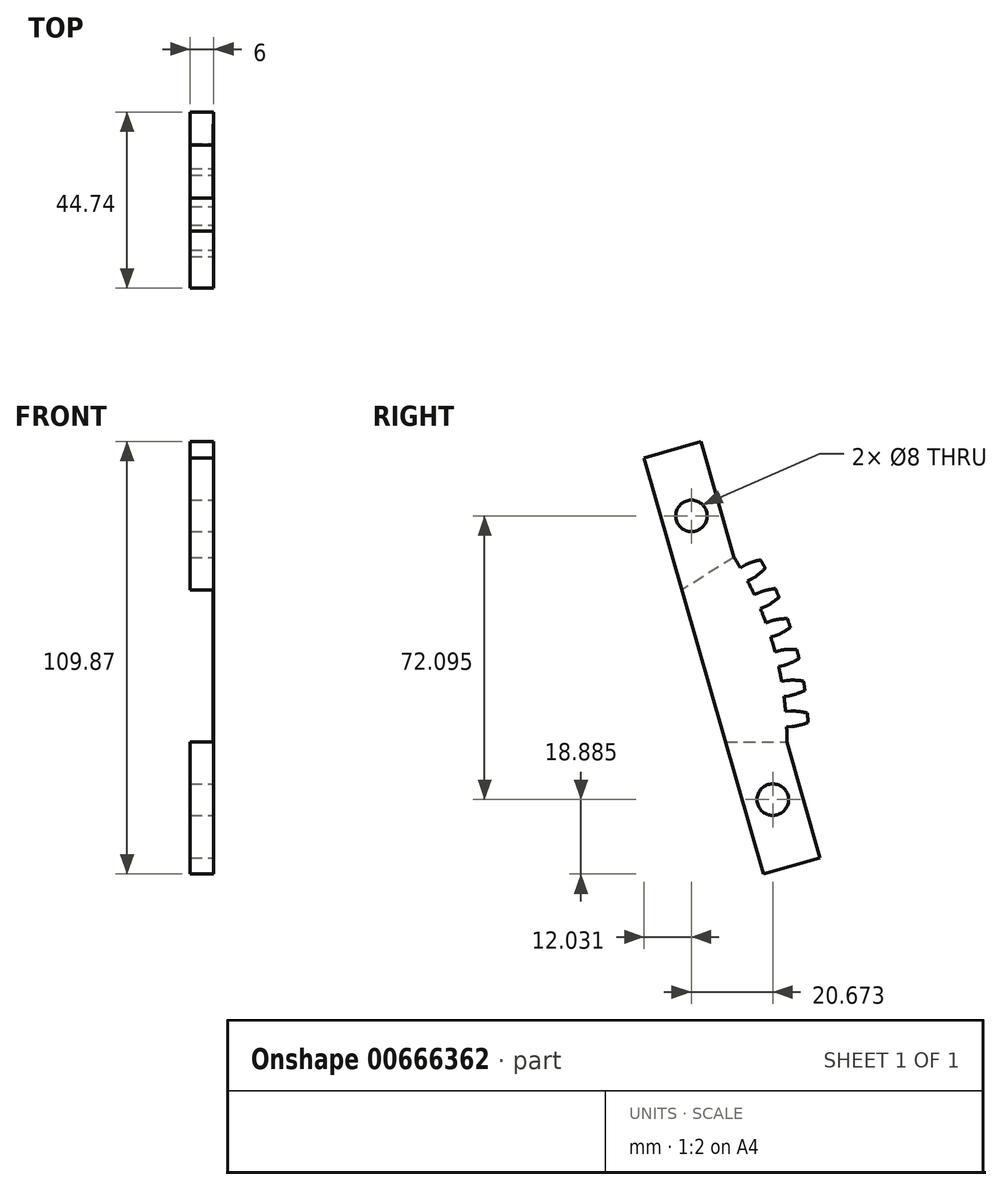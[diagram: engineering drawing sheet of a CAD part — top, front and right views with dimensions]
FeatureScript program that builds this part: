
annotation { "Feature Type Name" : "Feature", "Feature Type Description" : "" }
export const myFeature = defineFeature(function(context is Context, id is Id, definition is map)
    precondition{}
    {
        {
            assignVariable(context, id + "F0", {"name" : "NumberTeeth", "anyValue" : 72});
        }
        {
            assignVariable(context, id + "F1", {"name" : "GearThickness", "anyValue" : .236});
        }
        {
            var Q0;
            Q0=qCreatedBy(makeId("Right.planeOp"),FACE);
            var sketch = newSketch(context, id + "F2", { "sketchPlane" : qUnion([Q0])});
            skCircle(sketch, "E0", {"center": v(0, 0) * mm, "radius": 88.5 * mm});
            skCircle(sketch, "E1", {"center": v(0, 0) * mm, "radius": 89.9 * mm, "construction": true});
            skCircle(sketch, "E2", {"center": v(0, 0) * mm, "radius": 91.44 * mm, "construction": true});
            skCircle(sketch, "E3", {"center": v(0, 0) * mm, "radius": 93.98 * mm});
            skLineSegment(sketch, "E4", {"start": v(0, 0) * mm, "end": v(-89.9, 0) * mm, "construction": true});
            skLineSegment(sketch, "E5.1.0", {"start": v(0, 0) * mm, "end": v(-89.8, 4.5) * mm, "construction": true});
            skLineSegment(sketch, "E5.2.0", {"start": v(0, 0) * mm, "end": v(-89.46, 8.98) * mm, "construction": true});
            skLineSegment(sketch, "E5.3.0", {"start": v(0, 0) * mm, "end": v(-88.9, 13.44) * mm, "construction": true});
            skLineSegment(sketch, "E5.4.0", {"start": v(0, 0) * mm, "end": v(-88.12, 17.86) * mm, "construction": true});
            skLineSegment(sketch, "E5.5.0", {"start": v(0, 0) * mm, "end": v(-87.11, 22.24) * mm, "construction": true});
            skLineSegment(sketch, "E5.6.0", {"start": v(0, 0) * mm, "end": v(-85.9, 26.57) * mm, "construction": true});
            skLineSegment(sketch, "E5.7.0", {"start": v(0, 0) * mm, "end": v(-84.46, 30.83) * mm, "construction": true});
            skLineSegment(sketch, "E5.8.0", {"start": v(0, 0) * mm, "end": v(-82.81, 35.01) * mm, "construction": true});
            skLineSegment(sketch, "E5.9.0", {"start": v(0, 0) * mm, "end": v(-80.96, 39.1) * mm, "construction": true});
            skLineSegment(sketch, "E5.10.0", {"start": v(0, 0) * mm, "end": v(-78.9, 43.1) * mm, "construction": true});
            skLineSegment(sketch, "E5.11.0", {"start": v(0, 0) * mm, "end": v(-76.65, 47) * mm, "construction": true});
            skLineSegment(sketch, "E5.12.0", {"start": v(0, 0) * mm, "end": v(-74.2, 50.77) * mm, "construction": true});
            skLineSegment(sketch, "E5.13.0", {"start": v(0, 0) * mm, "end": v(-71.57, 54.41) * mm, "construction": true});
            skLineSegment(sketch, "E5.14.0", {"start": v(0, 0) * mm, "end": v(-68.77, 57.92) * mm, "construction": true});
            skLineSegment(sketch, "E5.anchor2", {"start": v(0, 0) * mm, "end": v(-68.77, 57.92) * mm, "construction": true});
            skLineSegment(sketch, "E6", {"start": v(-89.8, 4.5) * mm, "end": v(-90.02, 0) * mm, "construction": true});
            skLineSegment(sketch, "E7", {"start": v(-89.46, 8.98) * mm, "end": v(-90.36, 0.03) * mm, "construction": true});
            skLineSegment(sketch, "E8", {"start": v(-88.9, 13.44) * mm, "end": v(-90.91, 0.1) * mm, "construction": true});
            skLineSegment(sketch, "E9", {"start": v(-87.11, 22.24) * mm, "end": v(-92.67, 0.47) * mm, "construction": true});
            skLineSegment(sketch, "E10", {"start": v(-85.9, 26.57) * mm, "end": v(-93.86, 0.8) * mm, "construction": true});
            skLineSegment(sketch, "E11", {"start": v(-84.46, 30.83) * mm, "end": v(-95.25, 1.27) * mm, "construction": true});
            skLineSegment(sketch, "E12", {"start": v(-82.81, 35.01) * mm, "end": v(-96.82, 1.89) * mm, "construction": true});
            skLineSegment(sketch, "E13", {"start": v(-80.96, 39.1) * mm, "end": v(-98.56, 2.68) * mm, "construction": true});
            skLineSegment(sketch, "E14", {"start": v(-78.9, 43.1) * mm, "end": v(-100.45, 3.65) * mm, "construction": true});
            skLineSegment(sketch, "E15", {"start": v(-76.65, 47) * mm, "end": v(-102.5, 4.84) * mm, "construction": true});
            skLineSegment(sketch, "E16", {"start": v(-88.12, 17.86) * mm, "end": v(-91.69, 0.24) * mm, "construction": true});
            skLineSegment(sketch, "E17", {"start": v(-74.2, 50.77) * mm, "end": v(-104.66, 6.24) * mm, "construction": true});
            skLineSegment(sketch, "E18", {"start": v(-71.57, 54.41) * mm, "end": v(-106.94, 7.89) * mm, "construction": true});
            skLineSegment(sketch, "E19", {"start": v(-68.77, 57.92) * mm, "end": v(-109.31, 9.78) * mm, "construction": true});
            skLineSegment(sketch, "E20", {"start": v(0, 0) * mm, "end": v(-89.89, 1.96) * mm, "construction": true});
            skLineSegment(sketch, "E21", {"start": v(-88.5, 0) * mm, "end": v(-89.9, 0) * mm});
            skLineSegment(sketch, "E22.MirrorCS", {"start": v(-88.42, 3.86) * mm, "end": v(-89.82, 3.92) * mm});
            skFitSpline(sketch, "E23", {"points": [v(-89.9, 0) * mm, v(-90.02, 0) * mm, v(-90.36, 0.03) * mm, v(-90.91, 0.1) * mm, v(-91.69, 0.24) * mm, v(-92.67, 0.47) * mm, v(-93.86, 0.8) * mm, v(-95.25, 1.27) * mm, v(-96.82, 1.89) * mm, v(-98.56, 2.68) * mm, v(-100.45, 3.65) * mm, v(-102.5, 4.84) * mm, v(-104.66, 6.24) * mm, v(-106.94, 7.89) * mm, v(-109.31, 9.78) * mm], "startDerivative": vector(-0.31, 0) * mm, "endDerivative": vector(-3.2, 2.69) * mm});
            skLineSegment(sketch, "E24", {"start": v(-52.65, -37.94) * mm, "end": v(-109.31, 9.78) * mm, "construction": true});
            skFitSpline(sketch, "E25.MirrorCS", {"points": [v(-89.82, 3.92) * mm, v(-89.94, 3.92) * mm, v(-90.27, 3.91) * mm, v(-90.83, 3.86) * mm, v(-91.61, 3.76) * mm, v(-92.6, 3.58) * mm, v(-93.8, 3.3) * mm, v(-95.21, 2.89) * mm, v(-96.8, 2.34) * mm, v(-98.58, 1.63) * mm, v(-100.52, 0.73) * mm, v(-102.6, -0.36) * mm, v(-104.84, -1.67) * mm, v(-107.18, -3.22) * mm, v(-109.63, -5) * mm], "startDerivative": vector(-0.31, 0.01) * mm, "endDerivative": vector(-3.3, -2.55) * mm});
            skSolve(sketch);
        }
        {
            var Q0;
            {var subQ0=sQuery(id+"F2.wireOp",EDGE,"E0");var subQ27=makeQuery(id+"F2.imprint","INTERSECT",VERTEX,{"derivedFrom":[subQ0,sQuery(id+"F2.wireOp",EDGE,"10ea1024-8cf5-41f5-a75f-a634b86921f3.10.0")]});Q0=makeQuery(id+"F2.imprint","IMPRINT",FACE,{"disambiguationData":[TD([[makeQuery(id+"F2.imprint","IMPRINT",EDGE,{"disambiguationData":[TD([[subQ27,-1.0]])],"derivedFrom":subQ0}),1.0]])]});}
            var Q1;
            {var subQ0=sQuery(id+"F2.wireOp",EDGE,"10ea1024-8cf5-41f5-a75f-a634b86921f3.1.0");Q1=makeQuery(id+"F2.imprint","IMPRINT",FACE,{"disambiguationData":[TD([[makeQuery(id+"F2.imprint","IMPRINT",EDGE,{"derivedFrom":subQ0}),-1.0]])]});}
            var Q2;
            {var subQ7=sQuery(id+"F2.wireOp",EDGE,"10ea1024-8cf5-41f5-a75f-a634b86921f3.2.0");Q2=makeQuery(id+"F2.imprint","IMPRINT",FACE,{"disambiguationData":[TD([[makeQuery(id+"F2.imprint","IMPRINT",EDGE,{"derivedFrom":subQ7}),-1.0]])]});}
            var Q3;
            {var subQ8=sQuery(id+"F2.wireOp",EDGE,"10ea1024-8cf5-41f5-a75f-a634b86921f3.3.0");Q3=makeQuery(id+"F2.imprint","IMPRINT",FACE,{"disambiguationData":[TD([[makeQuery(id+"F2.imprint","IMPRINT",EDGE,{"derivedFrom":subQ8}),-1.0]])]});}
            var Q4;
            {var subQ2=sQuery(id+"F2.wireOp",EDGE,"10ea1024-8cf5-41f5-a75f-a634b86921f3.4.0");Q4=makeQuery(id+"F2.imprint","IMPRINT",FACE,{"disambiguationData":[TD([[makeQuery(id+"F2.imprint","IMPRINT",EDGE,{"derivedFrom":subQ2}),-1.0]])]});}
            var Q5;
            {var subQ8=sQuery(id+"F2.wireOp",EDGE,"10ea1024-8cf5-41f5-a75f-a634b86921f3.5.0");Q5=makeQuery(id+"F2.imprint","IMPRINT",FACE,{"disambiguationData":[TD([[makeQuery(id+"F2.imprint","IMPRINT",EDGE,{"derivedFrom":subQ8}),-1.0]])]});}
            var Q6;
            {var subQ3=sQuery(id+"F2.wireOp",EDGE,"10ea1024-8cf5-41f5-a75f-a634b86921f3.6.0");Q6=makeQuery(id+"F2.imprint","IMPRINT",FACE,{"disambiguationData":[TD([[makeQuery(id+"F2.imprint","IMPRINT",EDGE,{"derivedFrom":subQ3}),-1.0]])]});}
            var Q7;
            {var subQ0=sQuery(id+"F2.wireOp",EDGE,"10ea1024-8cf5-41f5-a75f-a634b86921f3.7.0");Q7=makeQuery(id+"F2.imprint","IMPRINT",FACE,{"disambiguationData":[TD([[makeQuery(id+"F2.imprint","IMPRINT",EDGE,{"derivedFrom":subQ0}),-1.0]])]});}
            var Q8;
            {var subQ5=sQuery(id+"F2.wireOp",EDGE,"10ea1024-8cf5-41f5-a75f-a634b86921f3.8.0");Q8=makeQuery(id+"F2.imprint","IMPRINT",FACE,{"disambiguationData":[TD([[makeQuery(id+"F2.imprint","IMPRINT",EDGE,{"derivedFrom":subQ5}),-1.0]])]});}
            var Q9;
            {var subQ1=sQuery(id+"F2.wireOp",EDGE,"10ea1024-8cf5-41f5-a75f-a634b86921f3.9.0");Q9=makeQuery(id+"F2.imprint","IMPRINT",FACE,{"disambiguationData":[TD([[makeQuery(id+"F2.imprint","IMPRINT",EDGE,{"derivedFrom":subQ1}),-1.0]])]});}
            var Q10;
            {var subQ5=sQuery(id+"F2.wireOp",EDGE,"10ea1024-8cf5-41f5-a75f-a634b86921f3.10.0");Q10=makeQuery(id+"F2.imprint","IMPRINT",FACE,{"disambiguationData":[TD([[makeQuery(id+"F2.imprint","IMPRINT",EDGE,{"derivedFrom":subQ5}),-1.0]])]});}
            var Q11;
            {var subQ8=sQuery(id+"F2.wireOp",EDGE,"10ea1024-8cf5-41f5-a75f-a634b86921f3.11.0");Q11=makeQuery(id+"F2.imprint","IMPRINT",FACE,{"disambiguationData":[TD([[makeQuery(id+"F2.imprint","IMPRINT",EDGE,{"derivedFrom":subQ8}),-1.0]])]});}
            var Q12;
            {var subQ2=sQuery(id+"F2.wireOp",EDGE,"10ea1024-8cf5-41f5-a75f-a634b86921f3.12.0");Q12=makeQuery(id+"F2.imprint","IMPRINT",FACE,{"disambiguationData":[TD([[makeQuery(id+"F2.imprint","IMPRINT",EDGE,{"derivedFrom":subQ2}),-1.0]])]});}
            var Q13;
            {var subQ3=sQuery(id+"F2.wireOp",EDGE,"10ea1024-8cf5-41f5-a75f-a634b86921f3.13.0");Q13=makeQuery(id+"F2.imprint","IMPRINT",FACE,{"disambiguationData":[TD([[makeQuery(id+"F2.imprint","IMPRINT",EDGE,{"derivedFrom":subQ3}),-1.0]])]});}
            var Q14;
            {var subQ0=sQuery(id+"F2.wireOp",EDGE,"10ea1024-8cf5-41f5-a75f-a634b86921f3.14.0");Q14=makeQuery(id+"F2.imprint","IMPRINT",FACE,{"disambiguationData":[TD([[makeQuery(id+"F2.imprint","IMPRINT",EDGE,{"derivedFrom":subQ0}),-1.0]])]});}
            var Q15;
            {var subQ6=sQuery(id+"F2.wireOp",EDGE,"10ea1024-8cf5-41f5-a75f-a634b86921f3.15.0");Q15=makeQuery(id+"F2.imprint","IMPRINT",FACE,{"disambiguationData":[TD([[makeQuery(id+"F2.imprint","IMPRINT",EDGE,{"derivedFrom":subQ6}),-1.0]])]});}
            var Q16;
            {var subQ5=sQuery(id+"F2.wireOp",EDGE,"10ea1024-8cf5-41f5-a75f-a634b86921f3.16.0");Q16=makeQuery(id+"F2.imprint","IMPRINT",FACE,{"disambiguationData":[TD([[makeQuery(id+"F2.imprint","IMPRINT",EDGE,{"derivedFrom":subQ5}),-1.0]])]});}
            var Q17;
            {var subQ7=sQuery(id+"F2.wireOp",EDGE,"10ea1024-8cf5-41f5-a75f-a634b86921f3.17.0");Q17=makeQuery(id+"F2.imprint","IMPRINT",FACE,{"disambiguationData":[TD([[makeQuery(id+"F2.imprint","IMPRINT",EDGE,{"derivedFrom":subQ7}),-1.0]])]});}
            var Q18;
            {var subQ5=sQuery(id+"F2.wireOp",EDGE,"10ea1024-8cf5-41f5-a75f-a634b86921f3.18.0");Q18=makeQuery(id+"F2.imprint","IMPRINT",FACE,{"disambiguationData":[TD([[makeQuery(id+"F2.imprint","IMPRINT",EDGE,{"derivedFrom":subQ5}),-1.0]])]});}
            var Q19;
            {var subQ8=sQuery(id+"F2.wireOp",EDGE,"10ea1024-8cf5-41f5-a75f-a634b86921f3.19.0");Q19=makeQuery(id+"F2.imprint","IMPRINT",FACE,{"disambiguationData":[TD([[makeQuery(id+"F2.imprint","IMPRINT",EDGE,{"derivedFrom":subQ8}),-1.0]])]});}
            var Q20;
            {var subQ8=sQuery(id+"F2.wireOp",EDGE,"E21");Q20=makeQuery(id+"F2.imprint","IMPRINT",FACE,{"disambiguationData":[TD([[makeQuery(id+"F2.imprint","IMPRINT",EDGE,{"derivedFrom":subQ8}),-1.0]])]});}
            extrude(context, id + "F3", {"entities" : qUnion([Q0, Q1, Q2, Q3, Q4, Q5, Q6, Q7, Q8, Q9, Q10, Q11, Q12, Q13, Q14, Q15, Q16, Q17, Q18, Q19, Q20]), "depth" : (getVariable(context, 'GearThickness')) * mm});
        }
        {
            var Q0;
            Q0=makeQuery(id+"F3.opExtrude","SWEPT_FACE",FACE,{"disambiguationData":[OSD([sQuery(id+"F2.wireOp",EDGE,"E25.MirrorCS")])]});
            var Q1;
            Q1=makeQuery(id+"F3.opExtrude","SWEPT_FACE",FACE,{"disambiguationData":[OSD([sQuery(id+"F2.wireOp",EDGE,"E23")])]});
            var Q2;
            Q2=makeQuery(id+"F3.opExtrude","SWEPT_FACE",FACE,{"disambiguationData":[OSD([sQuery(id+"F2.wireOp",EDGE,"E3")])]});
            var Q3;
            Q3=makeQuery(id+"F3.opExtrude","SWEPT_FACE",FACE,{"disambiguationData":[OSD([sQuery(id+"F2.wireOp",EDGE,"E22.MirrorCS")])]});
            var Q4;
            Q4=makeQuery(id+"F3.opExtrude","SWEPT_FACE",FACE,{"disambiguationData":[OSD([sQuery(id+"F2.wireOp",EDGE,"E21")])]});
            var Q5;
            Q5=makeQuery(id+"F3.opExtrude","SWEPT_FACE",FACE,{"disambiguationData":[OSD([sQuery(id+"F2.wireOp",EDGE,"E0")])]});
            circularPattern(context, id + "F4", {"faces" : qUnion([Q0, Q1, Q2, Q3, Q4]), "axis" : qUnion([Q5]), "angle" : 360 * degree, "instanceCount" : getVariable(context, 'NumberTeeth'), "equalSpace" : true, "patternType" : PatternType.FACE});
        }
        {
            var Q0;
            Q0=makeQuery(id+"F3.opExtrude","CAP_FACE",FACE,{"disambiguationData":[OSD([sQuery(id+"F2.wireOp",EDGE,"E0"),sQuery(id+"F2.wireOp",EDGE,"E3"),sQuery(id+"F2.wireOp",EDGE,"E21"),sQuery(id+"F2.wireOp",EDGE,"E22.MirrorCS"),sQuery(id+"F2.wireOp",EDGE,"E23"),sQuery(id+"F2.wireOp",EDGE,"E25.MirrorCS")])],"isStart":false});
            var sketch = newSketch(context, id + "F5", { "sketchPlane" : qUnion([Q0])});
            skArc(sketch, "E26", {"start": v(102.47, 0) * mm, "mid": v(-98.5, -28.24) * mm, "end": v(86.9, 54.3) * mm});
            skLineSegment(sketch, "E27", {"start": v(0, 0) * mm, "end": v(127.7, 79.8) * mm, "construction": true});
            skLineSegment(sketch, "E28", {"start": v(86.9, 54.3) * mm, "end": v(0, 0) * mm});
            skLineSegment(sketch, "E29", {"start": v(0, 0) * mm, "end": v(102.47, 0) * mm});
            skSolve(sketch);
        }
        {
            var Q0;
            Q0 = qSketchRegion(id + "F5", true);
            extrude(context, id + "F6", {"entities" : qUnion([Q0]), "operationType" : NewBodyOperationType.REMOVE, "oppositeDirection" : true, "depth" : 25.4 * mm, "offsetDistance" : 25.4 * mm});
        }
        {
            var Q0;
            Q0=makeQuery(id+"F3.opExtrude","CAP_FACE",FACE,{"disambiguationData":[OSD([sQuery(id+"F2.wireOp",EDGE,"E0"),sQuery(id+"F2.wireOp",EDGE,"E3"),sQuery(id+"F2.wireOp",EDGE,"E21"),sQuery(id+"F2.wireOp",EDGE,"E22.MirrorCS"),sQuery(id+"F2.wireOp",EDGE,"E23"),sQuery(id+"F2.wireOp",EDGE,"E25.MirrorCS")])],"isStart":false});
            var sketch = newSketch(context, id + "F7", { "sketchPlane" : qUnion([Q0])});
            skLineSegment(sketch, "E30", {"start": v(88.5, 0) * mm, "end": v(75.05, 46.9) * mm, "construction": true});
            skLineSegment(sketch, "E31", {"start": v(0, 0) * mm, "end": v(81.78, 23.45) * mm, "construction": true});
            skLineSegment(sketch, "E32", {"start": v(81.78, 23.45) * mm, "end": v(66.62, 76.32) * mm});
            skLineSegment(sketch, "E33", {"start": v(66.62, 76.32) * mm, "end": v(52.2, 72.18) * mm});
            skLineSegment(sketch, "E34", {"start": v(52.2, 72.18) * mm, "end": v(67.36, 19.31) * mm});
            skLineSegment(sketch, "E35.MirrorCS", {"start": v(82.52, -33.55) * mm, "end": v(67.36, 19.31) * mm});
            skLineSegment(sketch, "E36.MirrorCS", {"start": v(96.94, -29.42) * mm, "end": v(82.52, -33.55) * mm});
            skLineSegment(sketch, "E37.MirrorCS", {"start": v(81.78, 23.45) * mm, "end": v(96.94, -29.42) * mm});
            skCircle(sketch, "E38", {"center": v(84.9, -14.67) * mm, "radius": 4 * mm});
            skLineSegment(sketch, "E39", {"start": v(89.73, -31.49) * mm, "end": v(77.55, 11) * mm, "construction": true});
            skCircle(sketch, "E40.MirrorC", {"center": v(64.23, 57.43) * mm, "radius": 4 * mm});
            skSolve(sketch);
        }
        {
            var Q0;
            {var subQ3=sQuery(id+"F7.wireOp",EDGE,"E33");Q0=makeQuery(id+"F7.imprint","IMPRINT",FACE,{"disambiguationData":[TD([[makeQuery(id+"F7.imprint","IMPRINT",EDGE,{"derivedFrom":subQ3}),1.0]])]});}
            var Q1;
            {var subQ0=sQuery(id+"F7.wireOp",EDGE,"E36.MirrorCS");Q1=makeQuery(id+"F7.imprint","IMPRINT",FACE,{"disambiguationData":[TD([[makeQuery(id+"F7.imprint","IMPRINT",EDGE,{"derivedFrom":subQ0}),-1.0]])]});}
            extrude(context, id + "F8", {"entities" : qUnion([Q0, Q1]), "operationType" : NewBodyOperationType.ADD, "oppositeDirection" : true, "depth" : 6 * mm, "offsetDistance" : 25.4 * mm});
        }
        {
            var Q0;
            {var subQ0=sQuery(id+"F7.wireOp",EDGE,"E35.MirrorCS");var subQ1=sQuery(id+"F7.wireOp",EDGE,"E34");var subQ2=makeQuery(id+"F7.imprint","INTERSECT",VERTEX,{"derivedFrom":[subQ1,subQ0]});Q0=makeQuery(id+"F7.imprint","IMPRINT",FACE,{"disambiguationData":[TD([[makeQuery(id+"F7.imprint","IMPRINT",EDGE,{"disambiguationData":[TD([[subQ2,1.0]])],"derivedFrom":subQ1}),-1.0]])]});}
            extrude(context, id + "F9", {"entities" : qUnion([Q0]), "operationType" : NewBodyOperationType.REMOVE, "oppositeDirection" : true, "depth" : 25.4 * mm, "offsetDistance" : 25.4 * mm});
        }
    });
